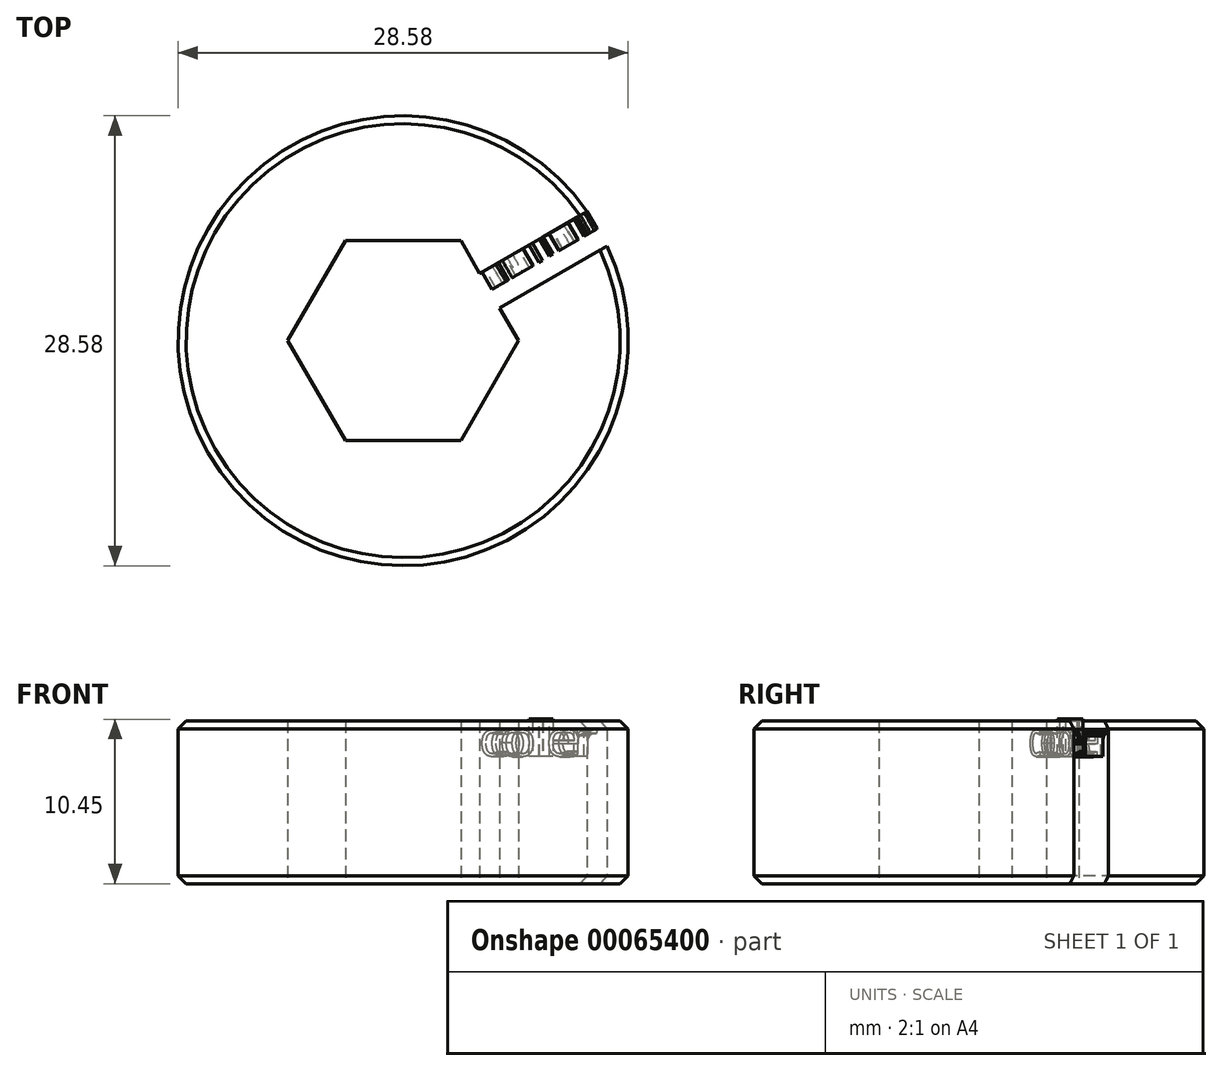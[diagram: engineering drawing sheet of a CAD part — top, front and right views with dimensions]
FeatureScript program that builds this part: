
annotation { "Feature Type Name" : "Feature", "Feature Type Description" : "" }
export const myFeature = defineFeature(function(context is Context, id is Id, definition is map)
    precondition{}
    {
        {
            var Q0;
            Q0=qCreatedBy(makeId("Top.planeOp"),FACE);
            var sketch = newSketch(context, id + "F0", { "sketchPlane" : qUnion([Q0])});
            skCircle(sketch, "E0", {"center": v(0, 0) * mm, "radius": 14.29 * mm});
            skCircle(sketch, "E1.cCircle", {"center": v(0, 0) * mm, "radius": 6.35 * mm, "construction": true});
            skLineSegment(sketch, "E1.0", {"start": v(3.67, 6.35) * mm, "end": v(7.33, 0) * mm});
            skLineSegment(sketch, "E1.1", {"start": v(7.33, 0) * mm, "end": v(3.67, -6.35) * mm});
            skLineSegment(sketch, "E1.2", {"start": v(3.67, -6.35) * mm, "end": v(-3.67, -6.35) * mm});
            skLineSegment(sketch, "E1.3", {"start": v(-3.67, -6.35) * mm, "end": v(-7.33, 0) * mm});
            skLineSegment(sketch, "E1.4", {"start": v(-7.33, 0) * mm, "end": v(-3.67, 6.35) * mm});
            skLineSegment(sketch, "E1.5", {"start": v(-3.67, 6.35) * mm, "end": v(3.67, 6.35) * mm});
            skPoint(sketch, "E1.0.midPoint", {"position": v(5.5, 3.17) * mm});
            skLineSegment(sketch, "E2", {"start": v(0, 0) * mm, "end": v(0, -14.29) * mm});
            skLineSegment(sketch, "E3", {"start": v(0, -14.29) * mm, "end": v(19.21, -14.29) * mm});
            skLineSegment(sketch, "E4", {"start": v(5.5, 3.18) * mm, "end": v(12.37, 7.14) * mm});
            skLineSegment(sketch, "E5", {"start": v(12.37, 7.14) * mm, "end": v(13, 6.04) * mm});
            skLineSegment(sketch, "E6", {"start": v(13, 6.04) * mm, "end": v(6.13, 2.08) * mm});
            skLineSegment(sketch, "E7", {"start": v(6.13, 2.08) * mm, "end": v(4.86, 4.27) * mm});
            skLineSegment(sketch, "E8", {"start": v(4.86, 4.27) * mm, "end": v(11.74, 8.24) * mm});
            skLineSegment(sketch, "E9", {"start": v(11.74, 8.24) * mm, "end": v(12.37, 7.14) * mm});
            skSolve(sketch);
        }
        {
            var Q0;
            {var subQ0=sQuery(id+"F0.wireOp",EDGE,"E1.3");Q0=makeQuery(id+"F0.imprint","IMPRINT",FACE,{"disambiguationData":[TD([[makeQuery(id+"F0.imprint","IMPRINT",EDGE,{"derivedFrom":subQ0}),1.0]])]});}
            var Q1;
            {var subQ1=sQuery(id+"F0.wireOp",EDGE,"E1.1");Q1=makeQuery(id+"F0.imprint","IMPRINT",FACE,{"disambiguationData":[TD([[makeQuery(id+"F0.imprint","IMPRINT",EDGE,{"derivedFrom":subQ1}),1.0]])]});}
            extrude(context, id + "F1", {"entities" : qUnion([Q0, Q1]), "depth" : 10.34 * mm});
        }
        {
            var Q0;
            Q0=makeQuery(id+"F1.opExtrude","CAP_EDGE",EDGE,{"disambiguationData":[OSD([sQuery(id+"F0.wireOp",EDGE,"E0")])],"isStart":false});
            var Q1;
            Q1=makeQuery(id+"F1.opExtrude","CAP_EDGE",EDGE,{"disambiguationData":[OSD([sQuery(id+"F0.wireOp",EDGE,"E0")])],"isStart":true});
            chamfer(context, id + "F2", {"entities" : qUnion([Q0, Q1]), "width" : 0.5 * mm, "tangentPropagation" : true});
        }
        {
            var Q0;
            Q0=makeQuery(id+"F1.opExtrude","SWEPT_FACE",FACE,{"disambiguationData":[OSD([sQuery(id+"F0.wireOp",EDGE,"E8")])]});
            var sketch = newSketch(context, id + "F3", { "sketchPlane" : qUnion([Q0])});
            skText(sketch, "E10", { "text": "coller\n", "fontName": "OpenSans-Regular.ttf"});
            const initialGuessF3  = {"E10": [0.00635, 0.0081, 1, 0, 0.00223]};
            skSetInitialGuess(sketch, initialGuessF3);
            skSolve(sketch);
        }
        {
            var Q0;
            Q0 = qSketchRegion(id + "F3", true);
            var Q1;
            {var subQ0=sQuery(id+"F3.wireOp",EDGE,"E10.sketch_text.stroke-36");Q1=makeQuery(id+"F3.imprint","IMPRINT",FACE,{"disambiguationData":[TD([[makeQuery(id+"F3.imprint","IMPRINT",EDGE,{"derivedFrom":subQ0}),-1.0]])]});}
            extrude(context, id + "F4", {"entities" : qUnion([Q0, Q1]), "operationType" : NewBodyOperationType.ADD, "depth" : 1.27 * mm});
        }
    });
